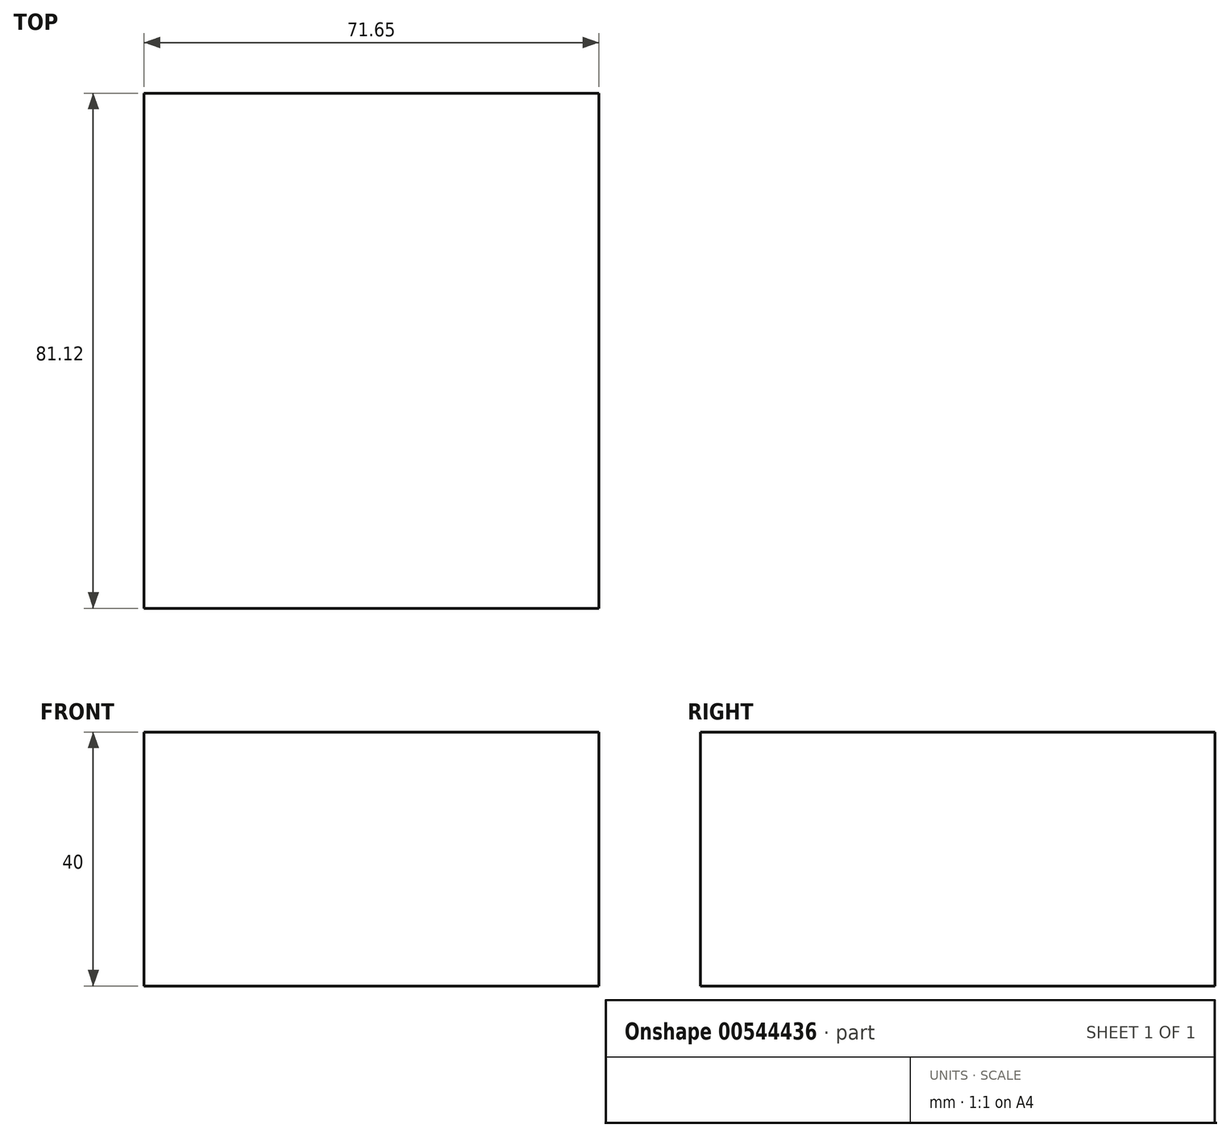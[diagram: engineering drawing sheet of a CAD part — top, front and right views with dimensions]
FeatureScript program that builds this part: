
annotation { "Feature Type Name" : "Feature", "Feature Type Description" : "" }
export const myFeature = defineFeature(function(context is Context, id is Id, definition is map)
    precondition{}
    {
        {
            var Q0;
            Q0=qCreatedBy(makeId("Top.planeOp"),FACE);
            var sketch = newSketch(context, id + "F0", { "sketchPlane" : qUnion([Q0])});
            skLineSegment(sketch, "E0.bottom", {"start": v(33.16, 40.56) * mm, "end": v(-38.49, 40.56) * mm});
            skLineSegment(sketch, "E0.top", {"start": v(33.16, -40.56) * mm, "end": v(-38.49, -40.56) * mm});
            skLineSegment(sketch, "E0.left", {"start": v(33.16, 40.56) * mm, "end": v(33.16, -40.56) * mm});
            skLineSegment(sketch, "E0.right", {"start": v(-38.49, 40.56) * mm, "end": v(-38.49, -40.56) * mm});
            skPoint(sketch, "E0.middle", {"position": v(-2.66, 0) * mm});
            skSolve(sketch);
        }
        {
            var Q0;
            Q0=makeQuery(id+"F0.imprint","IMPRINT",FACE,{"disambiguationData":[TD([[makeQuery(id+"F0.imprint","IMPRINT",EDGE,{"derivedFrom":sQuery(id+"F0.wireOp",EDGE,"E0.bottom")}),1.0]])]});
            var sketch = newSketch(context, id + "F1", { "sketchPlane" : qUnion([Q0])});
            skSolve(sketch);
        }
        {
            var Q0;
            Q0 = qSketchRegion(id + "F1", true);
            var Q1;
            Q1=makeQuery(id+"F0.imprint","IMPRINT",FACE,{"disambiguationData":[TD([[makeQuery(id+"F0.imprint","IMPRINT",EDGE,{"derivedFrom":sQuery(id+"F0.wireOp",EDGE,"E0.bottom")}),1.0]])]});
            extrude(context, id + "F2", {"entities" : qUnion([Q0, Q1]), "depth" : 40 * mm, "offsetDistance" : 25 * mm});
        }
    });
